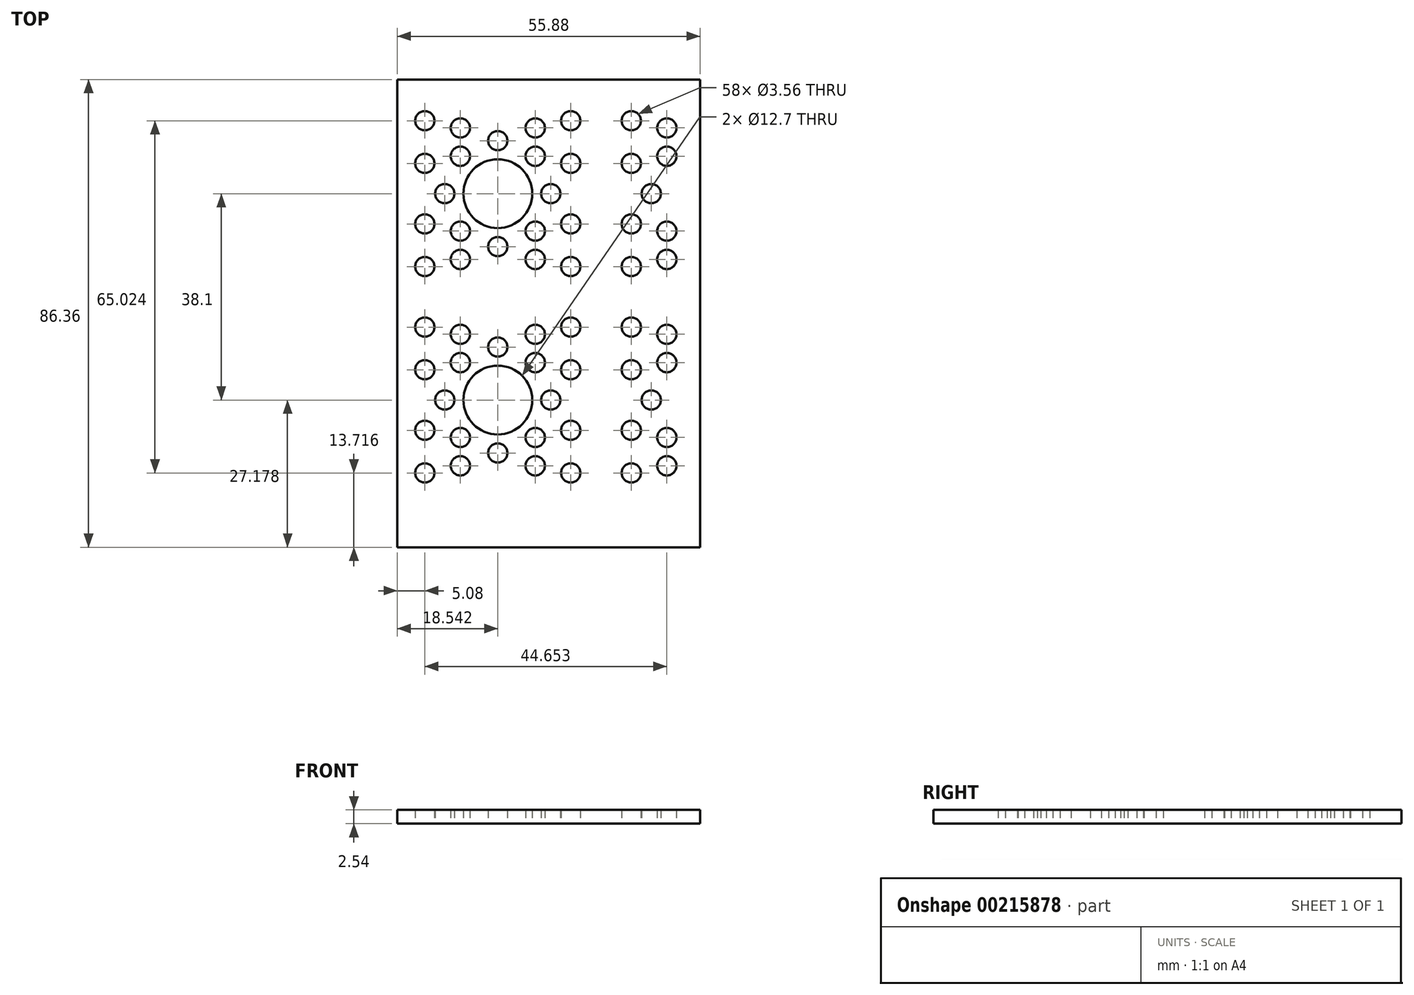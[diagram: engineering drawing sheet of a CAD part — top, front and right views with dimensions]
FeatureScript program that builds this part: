
annotation { "Feature Type Name" : "Feature", "Feature Type Description" : "" }
export const myFeature = defineFeature(function(context is Context, id is Id, definition is map)
    precondition{}
    {
        {
            var Q0;
            Q0=qCreatedBy(makeId("Top.planeOp"),FACE);
            var sketch = newSketch(context, id + "F0", { "sketchPlane" : qUnion([Q0])});
            skLineSegment(sketch, "E0.bottom", {"start": v(0, 0) * mm, "end": v(55.88, 0) * mm});
            skLineSegment(sketch, "E0.top", {"start": v(0, 86.36) * mm, "end": v(55.88, 86.36) * mm});
            skLineSegment(sketch, "E0.left", {"start": v(0, 0) * mm, "end": v(0, 86.36) * mm});
            skLineSegment(sketch, "E0.right", {"start": v(55.88, 0) * mm, "end": v(55.88, 86.36) * mm});
            skCircle(sketch, "E1", {"center": v(18.54, 65.28) * mm, "radius": 6.35 * mm});
            skCircle(sketch, "E2", {"center": v(18.54, 75.06) * mm, "radius": 1.78 * mm});
            skCircle(sketch, "E3", {"center": v(25.45, 77.42) * mm, "radius": 1.78 * mm});
            skCircle(sketch, "E4", {"center": v(25.45, 72.19) * mm, "radius": 1.78 * mm});
            skCircle(sketch, "E5", {"center": v(32, 78.74) * mm, "radius": 1.78 * mm});
            skCircle(sketch, "E6", {"center": v(32, 70.87) * mm, "radius": 1.78 * mm});
            skLineSegment(sketch, "E7", {"start": v(18.54, 65.28) * mm, "end": v(37.6, 65.28) * mm, "construction": true});
            skLineSegment(sketch, "E8", {"start": v(18.54, 65.28) * mm, "end": v(18.54, 56.81) * mm, "construction": true});
            skCircle(sketch, "E9.MirrorC", {"center": v(11.63, 77.42) * mm, "radius": 1.78 * mm});
            skCircle(sketch, "E10.MirrorC", {"center": v(5.08, 78.74) * mm, "radius": 1.78 * mm});
            skCircle(sketch, "E11.MirrorC", {"center": v(8.76, 65.28) * mm, "radius": 1.78 * mm});
            skCircle(sketch, "E12.MirrorC", {"center": v(11.63, 72.19) * mm, "radius": 1.78 * mm});
            skCircle(sketch, "E13.MirrorC", {"center": v(5.08, 70.87) * mm, "radius": 1.78 * mm});
            skCircle(sketch, "E14.MirrorC", {"center": v(5.08, 51.82) * mm, "radius": 1.78 * mm});
            skCircle(sketch, "E15.MirrorC", {"center": v(18.54, 55.5) * mm, "radius": 1.78 * mm});
            skCircle(sketch, "E16.MirrorC", {"center": v(11.63, 58.37) * mm, "radius": 1.78 * mm});
            skCircle(sketch, "E17.MirrorC", {"center": v(25.45, 53.14) * mm, "radius": 1.78 * mm});
            skCircle(sketch, "E18.MirrorC", {"center": v(11.63, 53.14) * mm, "radius": 1.78 * mm});
            skCircle(sketch, "E19.MirrorC", {"center": v(25.45, 58.37) * mm, "radius": 1.78 * mm});
            skCircle(sketch, "E20.MirrorC", {"center": v(32, 51.82) * mm, "radius": 1.78 * mm});
            skCircle(sketch, "E21.MirrorC", {"center": v(5.08, 59.7) * mm, "radius": 1.78 * mm});
            skCircle(sketch, "E22.MirrorC", {"center": v(32, 59.7) * mm, "radius": 1.78 * mm});
            skCircle(sketch, "E23.MirrorC", {"center": v(28.32, 65.28) * mm, "radius": 1.78 * mm});
            skLineSegment(sketch, "E24.MirrorCS", {"start": v(37.08, 0) * mm, "end": v(37.08, 86.36) * mm});
            skLineSegment(sketch, "E25", {"start": v(18.54, 65.28) * mm, "end": v(18.54, 46.23) * mm, "construction": true});
            skLineSegment(sketch, "E26", {"start": v(18.54, 46.23) * mm, "end": v(28.28, 46.23) * mm, "construction": true});
            skCircle(sketch, "E27.MirrorC", {"center": v(8.76, 27.18) * mm, "radius": 1.78 * mm});
            skCircle(sketch, "E28.MirrorC", {"center": v(11.63, 15.04) * mm, "radius": 1.78 * mm});
            skCircle(sketch, "E29.MirrorC", {"center": v(5.08, 21.59) * mm, "radius": 1.78 * mm});
            skCircle(sketch, "E30.MirrorC", {"center": v(25.45, 34.09) * mm, "radius": 1.78 * mm});
            skCircle(sketch, "E31.MirrorC", {"center": v(5.08, 32.77) * mm, "radius": 1.78 * mm});
            skCircle(sketch, "E32.MirrorC", {"center": v(25.45, 39.32) * mm, "radius": 1.78 * mm});
            skCircle(sketch, "E33.MirrorC", {"center": v(32, 21.59) * mm, "radius": 1.78 * mm});
            skCircle(sketch, "E34.MirrorC", {"center": v(32, 13.72) * mm, "radius": 1.78 * mm});
            skCircle(sketch, "E35.MirrorC", {"center": v(25.45, 15.04) * mm, "radius": 1.78 * mm});
            skCircle(sketch, "E36.MirrorC", {"center": v(11.63, 20.27) * mm, "radius": 1.78 * mm});
            skCircle(sketch, "E37.MirrorC", {"center": v(32, 32.77) * mm, "radius": 1.78 * mm});
            skCircle(sketch, "E38.MirrorC", {"center": v(28.32, 27.18) * mm, "radius": 1.78 * mm});
            skCircle(sketch, "E39.MirrorC", {"center": v(18.54, 17.4) * mm, "radius": 1.78 * mm});
            skLineSegment(sketch, "E40.MirrorCS", {"start": v(18.54, 27.18) * mm, "end": v(18.54, 35.65) * mm, "construction": true});
            skCircle(sketch, "E41.MirrorC", {"center": v(18.54, 36.96) * mm, "radius": 1.78 * mm});
            skCircle(sketch, "E42.MirrorC", {"center": v(5.08, 13.72) * mm, "radius": 1.78 * mm});
            skCircle(sketch, "E43.MirrorC", {"center": v(11.63, 39.32) * mm, "radius": 1.78 * mm});
            skCircle(sketch, "E44.MirrorC", {"center": v(11.63, 34.09) * mm, "radius": 1.78 * mm});
            skCircle(sketch, "E45.MirrorC", {"center": v(18.54, 27.18) * mm, "radius": 6.35 * mm});
            skCircle(sketch, "E46.MirrorC", {"center": v(25.45, 20.27) * mm, "radius": 1.78 * mm});
            skCircle(sketch, "E47.MirrorC", {"center": v(32, 40.64) * mm, "radius": 1.78 * mm});
            skCircle(sketch, "E48.MirrorC", {"center": v(5.08, 40.64) * mm, "radius": 1.78 * mm});
            skCircle(sketch, "E49", {"center": v(18.54, 46.23) * mm, "radius": 1.78 * mm, "construction": true});
            skLineSegment(sketch, "E50", {"start": v(37.6, 65.28) * mm, "end": v(37.6, 57.98) * mm, "construction": true});
            skCircle(sketch, "E51.MirrorC", {"center": v(49.73, 53.14) * mm, "radius": 1.78 * mm});
            skCircle(sketch, "E52.MirrorC", {"center": v(49.73, 58.37) * mm, "radius": 1.78 * mm});
            skCircle(sketch, "E53.MirrorC", {"center": v(46.86, 65.28) * mm, "radius": 1.78 * mm});
            skCircle(sketch, "E54.MirrorC", {"center": v(49.73, 72.19) * mm, "radius": 1.78 * mm});
            skCircle(sketch, "E55.MirrorC", {"center": v(49.73, 77.42) * mm, "radius": 1.78 * mm});
            skCircle(sketch, "E56.MirrorC", {"center": v(43.18, 59.7) * mm, "radius": 1.78 * mm});
            skCircle(sketch, "E57.MirrorC", {"center": v(43.18, 70.87) * mm, "radius": 1.78 * mm});
            skCircle(sketch, "E58.MirrorC", {"center": v(43.18, 78.74) * mm, "radius": 1.78 * mm});
            skCircle(sketch, "E59.MirrorC", {"center": v(43.18, 51.82) * mm, "radius": 1.78 * mm});
            skCircle(sketch, "E60.MirrorC", {"center": v(46.86, 27.18) * mm, "radius": 1.78 * mm});
            skCircle(sketch, "E61.MirrorC", {"center": v(49.73, 34.09) * mm, "radius": 1.78 * mm});
            skCircle(sketch, "E62.MirrorC", {"center": v(49.73, 20.27) * mm, "radius": 1.78 * mm});
            skCircle(sketch, "E63.MirrorC", {"center": v(49.73, 15.04) * mm, "radius": 1.78 * mm});
            skCircle(sketch, "E64.MirrorC", {"center": v(49.73, 39.32) * mm, "radius": 1.78 * mm});
            skCircle(sketch, "E65.MirrorC", {"center": v(43.18, 21.59) * mm, "radius": 1.78 * mm});
            skCircle(sketch, "E66.MirrorC", {"center": v(43.18, 13.72) * mm, "radius": 1.78 * mm});
            skCircle(sketch, "E67.MirrorC", {"center": v(43.18, 32.77) * mm, "radius": 1.78 * mm});
            skCircle(sketch, "E68.MirrorC", {"center": v(43.18, 40.64) * mm, "radius": 1.78 * mm});
            skSolve(sketch);
        }
        {
            var Q0;
            Q0=qSketchRegion(id+"F0",true);
            extrude(context, id + "F1", {"entities" : qUnion([Q0]), "depth" : 2.54 * mm});
        }
    });
